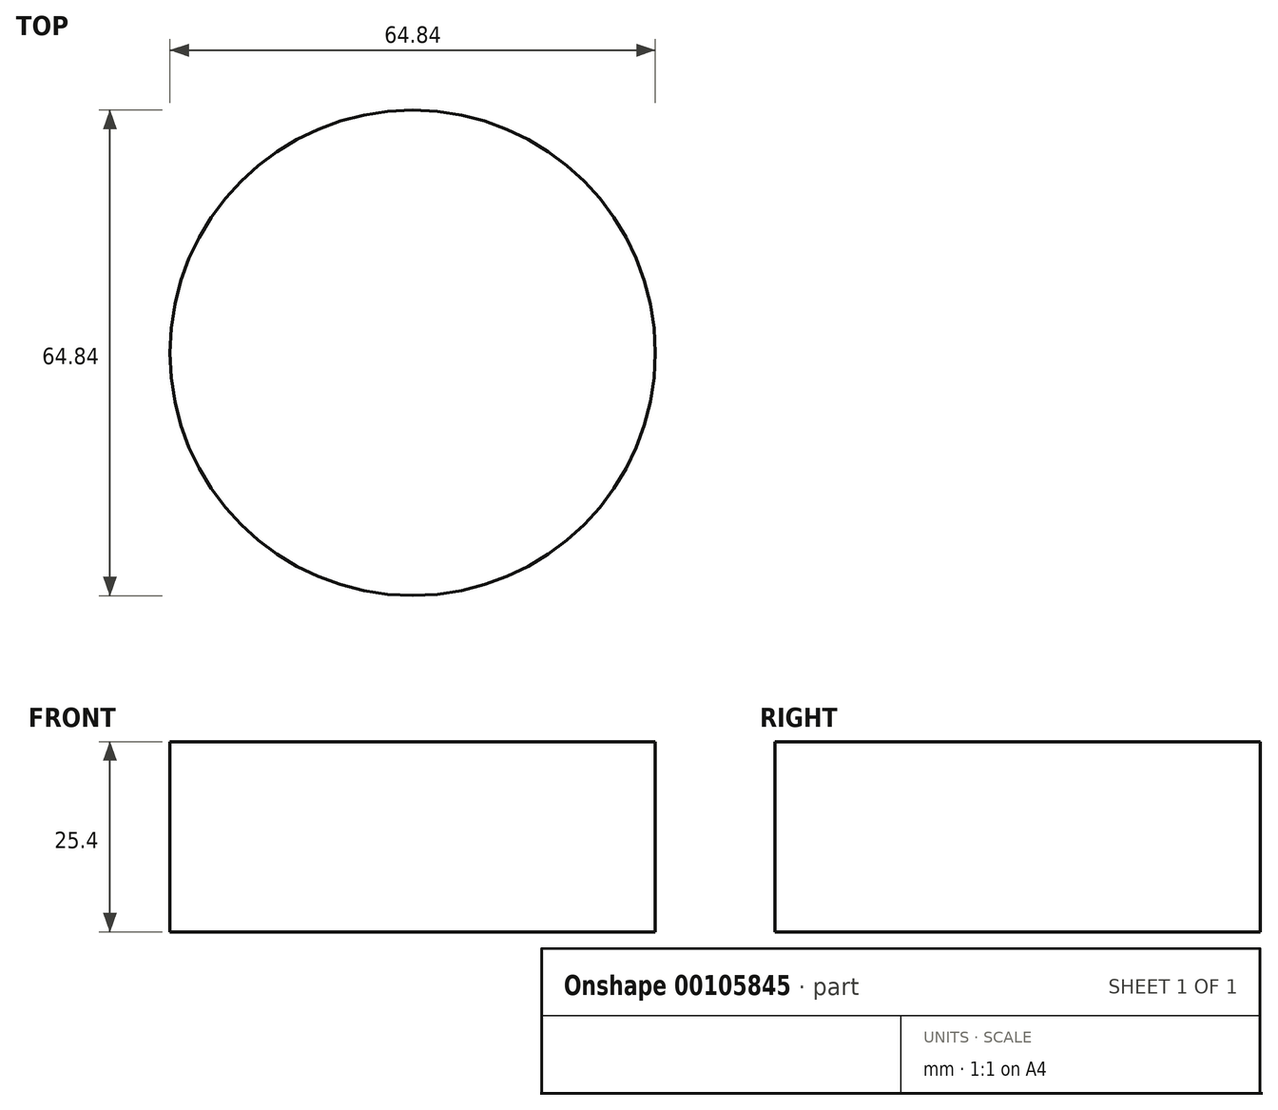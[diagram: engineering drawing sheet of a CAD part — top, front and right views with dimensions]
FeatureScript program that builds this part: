
annotation { "Feature Type Name" : "Feature", "Feature Type Description" : "" }
export const myFeature = defineFeature(function(context is Context, id is Id, definition is map)
    precondition{}
    {
        {
            var Q0;
            Q0=qCreatedBy(makeId("Top.planeOp"),FACE);
            var sketch = newSketch(context, id + "F0", { "sketchPlane" : qUnion([Q0])});
            skCircle(sketch, "E0", {"center": v(0, 0) * mm, "radius": 32.42 * mm});
            skSolve(sketch);
        }
        {
            var Q0;
            Q0=sQuery(id+"F0.wireOp",EDGE,"E0");
            extrude(context, id + "F1", {"bodyType" : ToolBodyType.SURFACE, "surfaceEntities" : qUnion([Q0]), "endBound" : BoundingType.SYMMETRIC, "depth" : 25.4 * mm});
        }
    });
